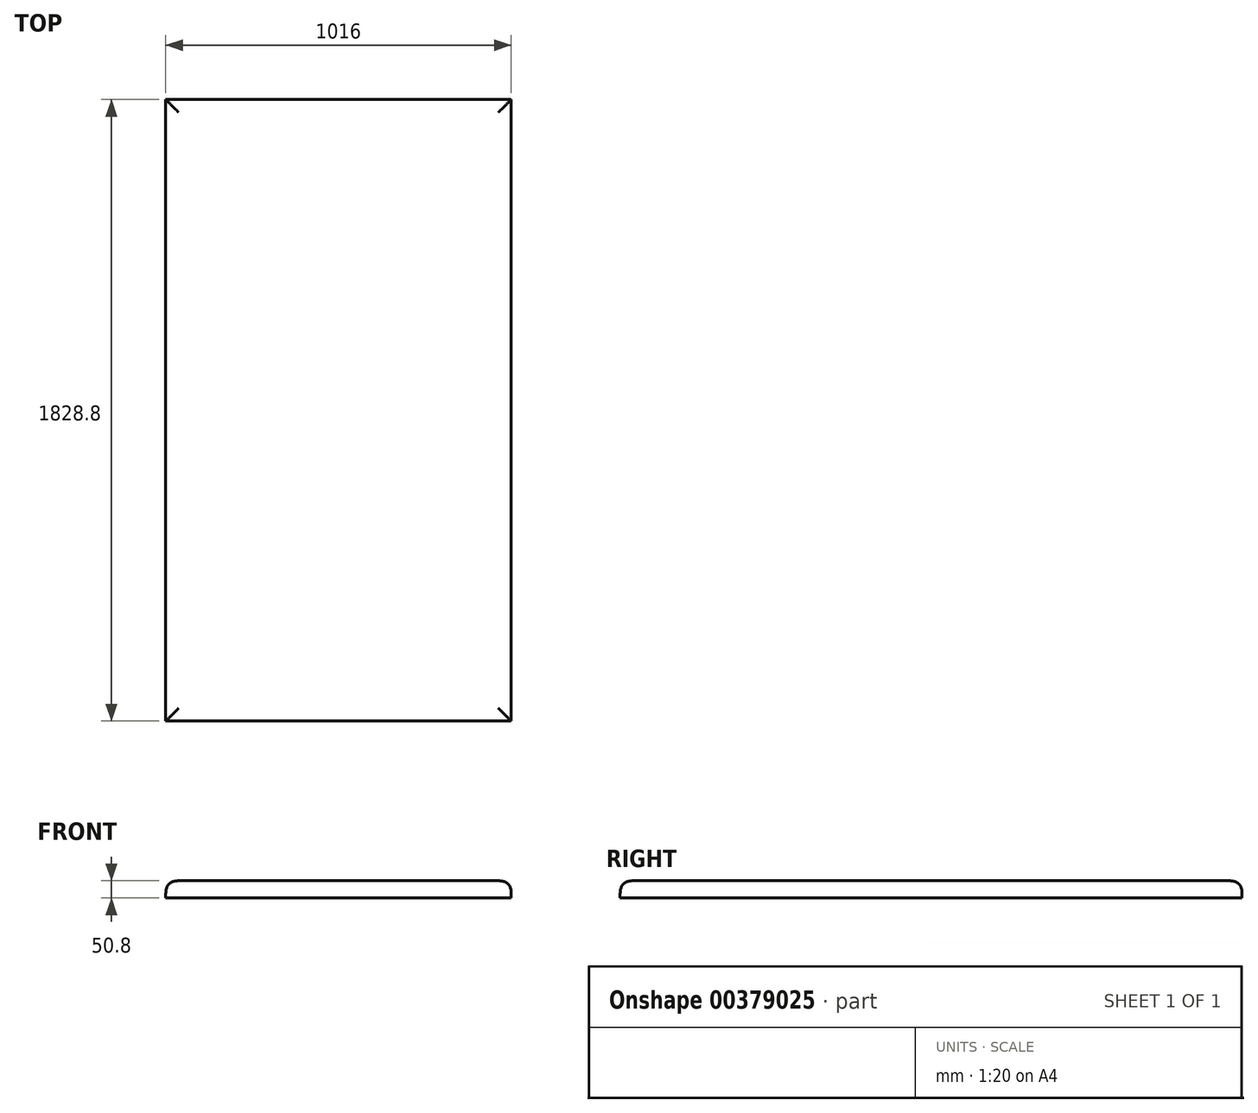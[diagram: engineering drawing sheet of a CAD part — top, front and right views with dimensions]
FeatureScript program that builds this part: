
annotation { "Feature Type Name" : "Feature", "Feature Type Description" : "" }
export const myFeature = defineFeature(function(context is Context, id is Id, definition is map)
    precondition{}
    {
        {
            var Q0;
            Q0=qCreatedBy(makeId("Top.planeOp"),FACE);
            var sketch = newSketch(context, id + "F0", { "sketchPlane" : qUnion([Q0])});
            skLineSegment(sketch, "E0.bottom", {"start": v(-554, 894.88) * mm, "end": v(462, 894.88) * mm});
            skLineSegment(sketch, "E0.top", {"start": v(-554, -933.92) * mm, "end": v(462, -933.92) * mm});
            skLineSegment(sketch, "E0.left", {"start": v(-554, 894.88) * mm, "end": v(-554, -933.92) * mm});
            skLineSegment(sketch, "E0.right", {"start": v(462, 894.88) * mm, "end": v(462, -933.92) * mm});
            skSolve(sketch);
        }
        {
            var Q0;
            Q0 = qSketchRegion(id + "F0", true);
            extrude(context, id + "F1", {"entities" : qUnion([Q0]), "depth" : 50.8 * mm});
        }
        {
            var Q0;
            Q0=makeQuery(id+"F1.opExtrude","CAP_FACE",FACE,{"disambiguationData":[OSD([sQuery(id+"F0.wireOp",EDGE,"E0.bottom"),sQuery(id+"F0.wireOp",EDGE,"E0.top"),sQuery(id+"F0.wireOp",EDGE,"E0.left"),sQuery(id+"F0.wireOp",EDGE,"E0.right")])],"isStart":false});
            var Q1;
            Q1=makeQuery(id+"F1.opExtrude","CAP_EDGE",EDGE,{"disambiguationData":[OSD([sQuery(id+"F0.wireOp",EDGE,"E0.left")])],"isStart":false});
            var Q2;
            Q2=makeQuery(id+"F1.opExtrude","CAP_EDGE",EDGE,{"disambiguationData":[OSD([sQuery(id+"F0.wireOp",EDGE,"E0.right")])],"isStart":false});
            var Q3;
            Q3=makeQuery(id+"F1.opExtrude","CAP_EDGE",EDGE,{"disambiguationData":[OSD([sQuery(id+"F0.wireOp",EDGE,"E0.top")])],"isStart":false});
            fillet(context, id + "F2", {"entities" : qUnion([Q0, Q1, Q2, Q3]), "radius" : 38.1 * mm, "tangentPropagation" : true, "rho" : 0.5, "crossSection" : FilletCrossSection.CONIC, "allowEdgeOverflow" : false});
        }
    });
